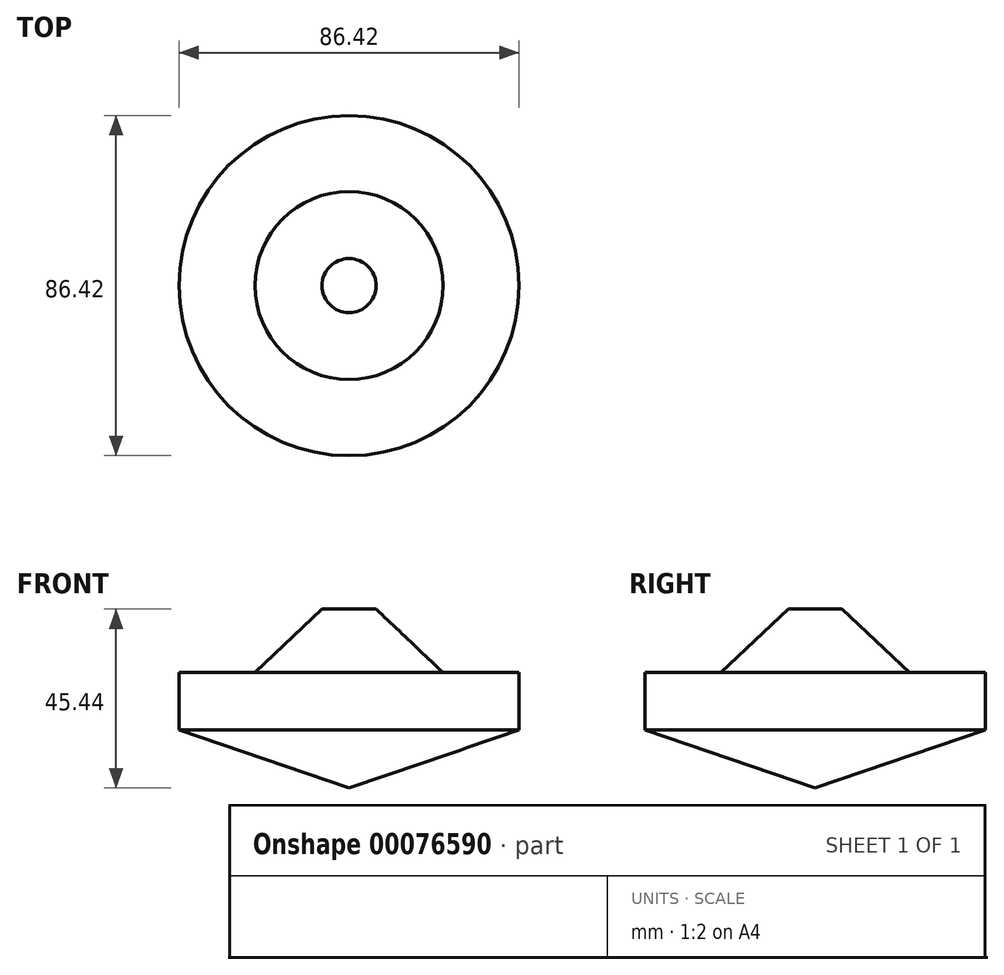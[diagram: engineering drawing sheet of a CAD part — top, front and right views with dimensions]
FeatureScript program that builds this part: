
annotation { "Feature Type Name" : "Feature", "Feature Type Description" : "" }
export const myFeature = defineFeature(function(context is Context, id is Id, definition is map)
    precondition{}
    {
        {
            var Q0;
            Q0=qCreatedBy(makeId("Front.planeOp"),FACE);
            var sketch = newSketch(context, id + "F0", { "sketchPlane" : qUnion([Q0])});
            skLineSegment(sketch, "E0", {"start": v(0, 0) * mm, "end": v(43.2, 14.74) * mm});
            skLineSegment(sketch, "E1", {"start": v(43.2, 14.74) * mm, "end": v(43.2, 29.35) * mm});
            skLineSegment(sketch, "E2", {"start": v(23.9, 29.35) * mm, "end": v(43.2, 29.35) * mm});
            skLineSegment(sketch, "E3", {"start": v(23.9, 29.35) * mm, "end": v(6.85, 45.44) * mm});
            skLineSegment(sketch, "E4", {"start": v(6.85, 45.44) * mm, "end": v(0, 45.44) * mm});
            skLineSegment(sketch, "E5", {"start": v(0, 45.44) * mm, "end": v(0, 0) * mm});
            skSolve(sketch);
        }
        {
            var Q0;
            Q0 = qSketchRegion(id + "F0", true);
            var Q1;
            Q1=sQuery(id+"F0.wireOp",EDGE,"E5");
            revolve(context, id + "F1", {"entities" : qUnion([Q0]), "axis" : qUnion([Q1]), "revolveType" : RevolveType.FULL});
        }
    });
